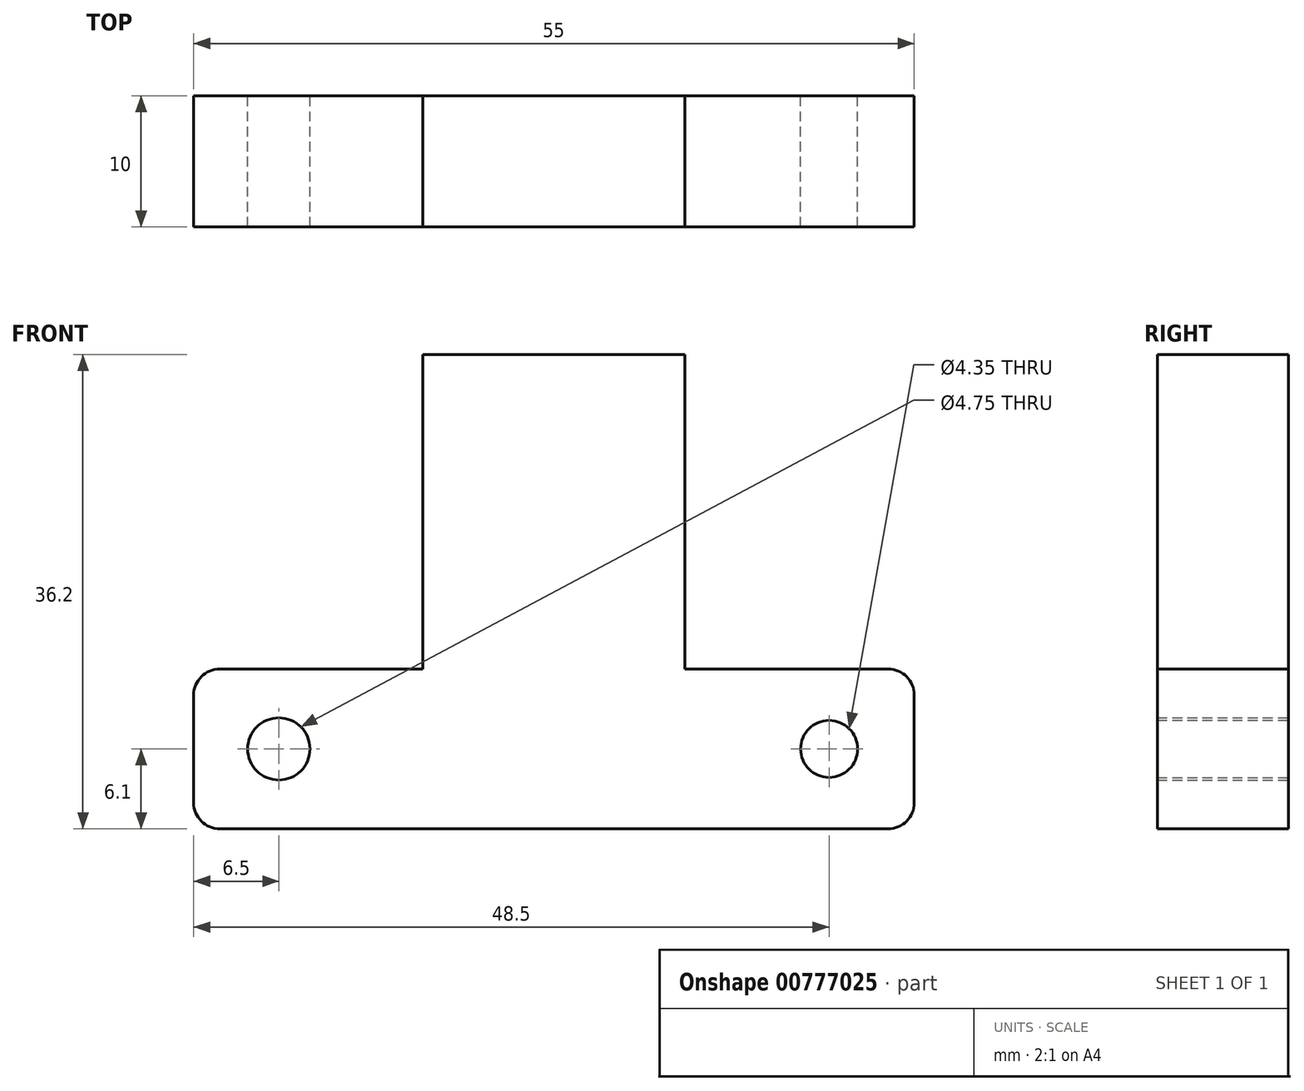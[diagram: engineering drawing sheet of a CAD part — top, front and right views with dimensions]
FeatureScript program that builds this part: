
annotation { "Feature Type Name" : "Feature", "Feature Type Description" : "" }
export const myFeature = defineFeature(function(context is Context, id is Id, definition is map)
    precondition{}
    {
        {
            var Q0;
            Q0=qCreatedBy(makeId("Front.planeOp"),FACE);
            var sketch = newSketch(context, id + "F0", { "sketchPlane" : qUnion([Q0])});
            skLineSegment(sketch, "E0.bottom", {"start": v(-27.5, 6.1) * mm, "end": v(27.5, 6.1) * mm});
            skLineSegment(sketch, "E0.top", {"start": v(-27.5, -6.1) * mm, "end": v(27.5, -6.1) * mm});
            skLineSegment(sketch, "E0.left", {"start": v(-27.5, 6.1) * mm, "end": v(-27.5, -6.1) * mm});
            skLineSegment(sketch, "E0.right", {"start": v(27.5, 6.1) * mm, "end": v(27.5, -6.1) * mm});
            skCircle(sketch, "E1", {"center": v(21, 0) * mm, "radius": 2.18 * mm});
            skCircle(sketch, "E2", {"center": v(-21, 0) * mm, "radius": 2.37 * mm});
            skSolve(sketch);
        }
        {
            var Q0;
            Q0=qSketchRegion(id+"F0",true);
            extrude(context, id + "F1", {"entities" : qUnion([Q0]), "depth" : 10 * mm, "offsetDistance" : 25 * mm});
        }
        {
            var Q0;
            Q0=makeQuery(id+"F1.opExtrude","SWEPT_FACE",FACE,{"disambiguationData":[OSD([sQuery(id+"F0.wireOp",EDGE,"E0.bottom")])]});
            var sketch = newSketch(context, id + "F2", { "sketchPlane" : qUnion([Q0])});
            skLineSegment(sketch, "E3.bottom", {"start": v(-10, 0) * mm, "end": v(10, 0) * mm});
            skLineSegment(sketch, "E3.top", {"start": v(-10, -10) * mm, "end": v(10, -10) * mm});
            skLineSegment(sketch, "E3.left", {"start": v(-10, 0) * mm, "end": v(-10, -10) * mm});
            skLineSegment(sketch, "E3.right", {"start": v(10, 0) * mm, "end": v(10, -10) * mm});
            skSolve(sketch);
        }
        {
            var Q0;
            Q0=qSketchRegion(id+"F2",true);
            extrude(context, id + "F3", {"entities" : qUnion([Q0]), "operationType" : NewBodyOperationType.ADD, "flatOperationType" : FlatOperationType.REMOVE, "depth" : 24 * mm, "offsetDistance" : 25 * mm, "domain" : OperationDomain.MODEL});
        }
        {
            var Q0;
            Q0=makeQuery(id+"F3.opExtrude","CAP_EDGE",EDGE,{"disambiguationData":[OSD([sQuery(id+"F2.wireOp",EDGE,"E3.right")])],"isStart":true});
            var Q1;
            Q1=makeQuery(id+"F1.opExtrude","SWEPT_EDGE",EDGE,{"disambiguationData":[OSD([sQuery(id+"F0.wireOp",EDGE,"E0.bottom"),sQuery(id+"F0.wireOp",EDGE,"E0.right")])]});
            var Q2;
            Q2=makeQuery(id+"F1.opExtrude","SWEPT_EDGE",EDGE,{"disambiguationData":[OSD([sQuery(id+"F0.wireOp",EDGE,"E0.top"),sQuery(id+"F0.wireOp",EDGE,"E0.right")])]});
            var Q3;
            {var subQ0=sQuery(id+"F2.wireOp",EDGE,"E3.right");Q3=makeQuery(id+"FlKPv2pDkQqTPje_1.opChamfer","BLEND_EDGE",EDGE,{"blendedFrom":[makeQuery(id+"F3.opExtrude","CAP_EDGE",EDGE,{"disambiguationData":[OSD([subQ0])],"isStart":false}),makeQuery(id+"F3.opExtrude","SWEPT_FACE",FACE,{"disambiguationData":[OSD([subQ0])]})],"blendedInto":[makeQuery(id+"F3.opExtrude","SWEPT_FACE",FACE,{"disambiguationData":[OSD([subQ0])]})]});}
            var Q4;
            {var subQ0=sQuery(id+"F2.wireOp",EDGE,"E3.left");Q4=makeQuery(id+"FlKPv2pDkQqTPje_1.opChamfer","BLEND_EDGE",EDGE,{"blendedFrom":[makeQuery(id+"F3.opExtrude","CAP_EDGE",EDGE,{"disambiguationData":[OSD([subQ0])],"isStart":false}),makeQuery(id+"F3.opExtrude","SWEPT_FACE",FACE,{"disambiguationData":[OSD([subQ0])]})],"blendedInto":[makeQuery(id+"F3.opExtrude","SWEPT_FACE",FACE,{"disambiguationData":[OSD([subQ0])]})]});}
            var Q5;
            Q5=makeQuery(id+"F3.opExtrude","CAP_EDGE",EDGE,{"disambiguationData":[OSD([sQuery(id+"F2.wireOp",EDGE,"E3.left")])],"isStart":true});
            var Q6;
            Q6=makeQuery(id+"F1.opExtrude","SWEPT_EDGE",EDGE,{"disambiguationData":[OSD([sQuery(id+"F0.wireOp",EDGE,"E0.bottom"),sQuery(id+"F0.wireOp",EDGE,"E0.left")])]});
            var Q7;
            Q7=makeQuery(id+"F1.opExtrude","SWEPT_EDGE",EDGE,{"disambiguationData":[OSD([sQuery(id+"F0.wireOp",EDGE,"E0.top"),sQuery(id+"F0.wireOp",EDGE,"E0.left")])]});
            fillet(context, id + "F4", {"entities" : qUnion([Q0, Q1, Q2, Q3, Q4, Q5, Q6, Q7]), "radius" : 2 * mm, "tangentPropagation" : true, "allowEdgeOverflow" : false});
        }
    });
